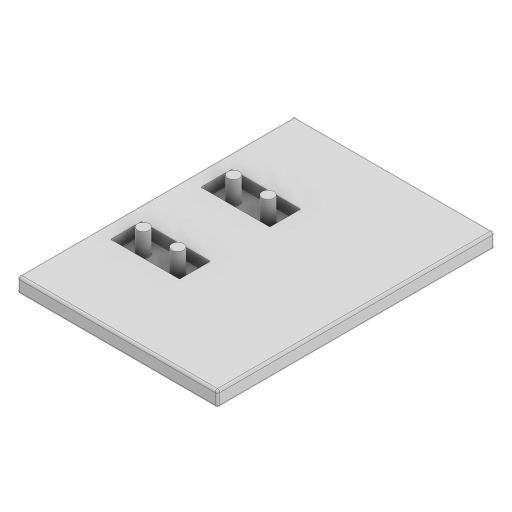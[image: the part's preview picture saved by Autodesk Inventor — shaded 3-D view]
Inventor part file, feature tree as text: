
AUTODESK INVENTOR PART (.ipt)
format: ipt  version: 2024 (Build 280153000, 153)  size: 212,992 bytes
history: native  units: mm
features: extrude x4, sketch x3, fillet x2
ambient origin geometry x8: Origin, YZ Plane, XZ Plane, XY Plane, X Axis, Y Axis, Z Axis, Center Point
bodies: Solid1 (feature_tree)
feature tree (9):
  sketch  "Sketch1"  dims[d0=260.0mm d1=360.0mm]
  extrude  "Extrusion1"  Depth=360.0mm
  extrude  "Extrusion2"  Depth=40.0mm
  extrude  "Extrusion3"  Depth=15.0mm
  sketch  "Sketch2"  dims[d2=89.4mm d3=40.0mm]
  extrude  "Extrusion5"  Depth=15.0mm
  fillet  "Fillet1"  Radius=22.35mm
  fillet  "Fillet2"  Radius=15.0mm
  sketch  "Sketch4"  dims[d4=89.4mm d5=40.0mm d8=15.0mm d9=15.0mm d11=22.35mm d12=15.0mm d13=15.0mm d14=22.35mm d15=22.35mm d16=22.35mm d17=20.0mm d18=20.0mm d19=0.0mm d20=5.0mm d21=0.0mm d22=35.0mm d23=0.0mm d39=15.0mm d40=10.0mm d41=20.0mm d42=20.0mm d43=15.0mm d44=10.0mm d45=15.0mm d46=10.0mm d47=15.0mm d48=10.0mm d49=20.0mm d50=20.0mm d51=20.0mm d52=20.0mm d53=20.0mm d54=20.0mm d55=1.0mm d56=0.0mm d57=3.0mm d61=117.2mm d62=101.4mm d63=101.4mm d64=1.0mm]
